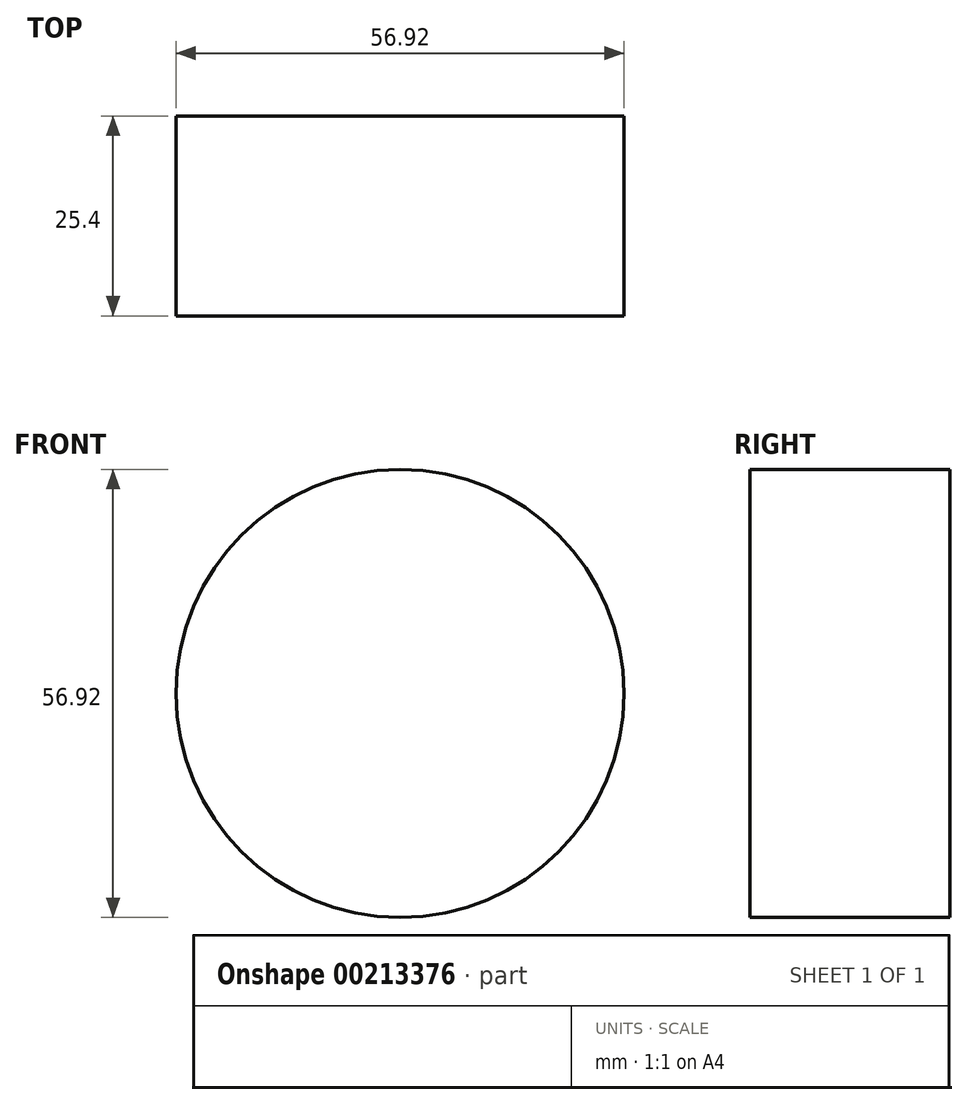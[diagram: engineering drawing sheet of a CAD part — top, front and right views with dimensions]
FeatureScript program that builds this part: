
annotation { "Feature Type Name" : "Feature", "Feature Type Description" : "" }
export const myFeature = defineFeature(function(context is Context, id is Id, definition is map)
    precondition{}
    {
        {
            var Q0;
            Q0=qCreatedBy(makeId("Front.planeOp"),FACE);
            var sketch = newSketch(context, id + "F0", { "sketchPlane" : qUnion([Q0])});
            skCircle(sketch, "E0", {"center": v(0, 0) * mm, "radius": 28.46 * mm});
            skSolve(sketch);
        }
        {
            var Q0;
            Q0=makeQuery(id+"F0.imprint","IMPRINT",FACE,{"disambiguationData":[TD([[makeQuery(id+"F0.imprint","IMPRINT",EDGE,{"derivedFrom":sQuery(id+"F0.wireOp",EDGE,"E0")}),1.0]])]});
            extrude(context, id + "F1", {"entities" : qUnion([Q0]), "depth" : 25.4 * mm, "offsetDistance" : 25.4 * mm});
        }
    });
